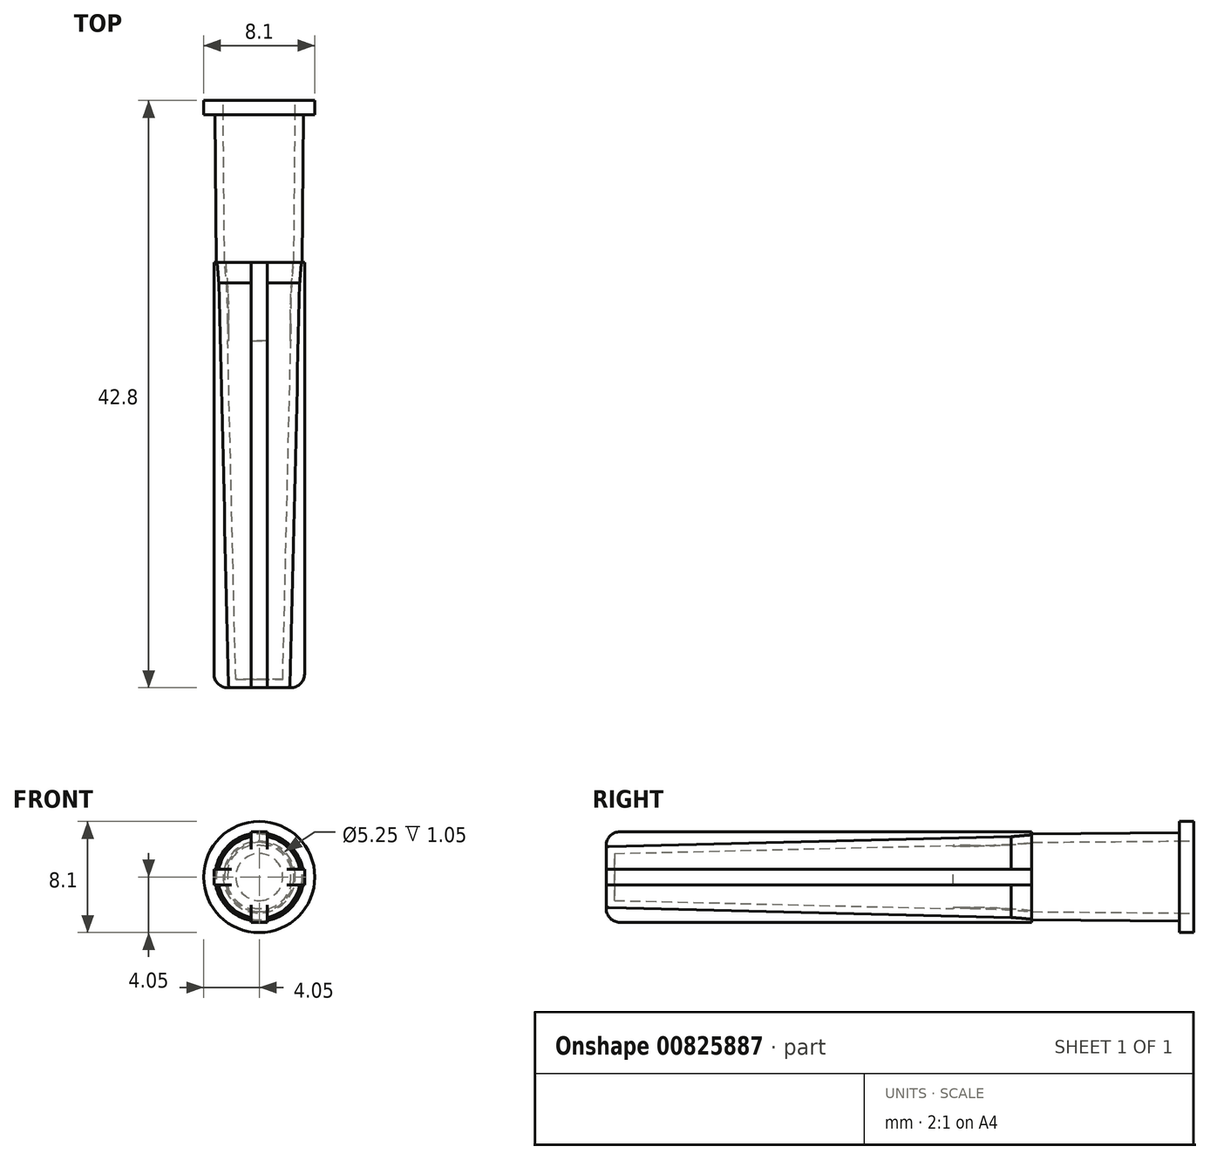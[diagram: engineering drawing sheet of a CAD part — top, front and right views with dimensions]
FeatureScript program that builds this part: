
annotation { "Feature Type Name" : "Feature", "Feature Type Description" : "" }
export const myFeature = defineFeature(function(context is Context, id is Id, definition is map)
    precondition{}
    {
        {
            var Q0;
            Q0=qCreatedBy(makeId("Front.planeOp"),FACE);
            var sketch = newSketch(context, id + "F0", { "sketchPlane" : qUnion([Q0])});
            skCircle(sketch, "E0", {"center": v(0, 0) * mm, "radius": 3.23 * mm});
            skSolve(sketch);
        }
        {
            var Q0;
            Q0=qCreatedBy(makeId("Front.planeOp"),FACE);
            cPlane(context, id + "F1", {"entities" : qUnion([Q0]), "cplaneType" : CPlaneType.OFFSET, "offset" : 10.75 * mm, "width" : 150 * mm, "height" : 150 * mm});
        }
        {
            var Q0;
            Q0=qCreatedBy(id+"F1.planeOp",FACE);
            var sketch = newSketch(context, id + "F2", { "sketchPlane" : qUnion([Q0])});
            skCircle(sketch, "E1", {"center": v(0, 0) * mm, "radius": 3.12 * mm});
            skSolve(sketch);
        }
        {
            var Q0;
            Q0=makeQuery(id+"F0.imprint","IMPRINT",FACE,{"disambiguationData":[TD([[makeQuery(id+"F0.imprint","IMPRINT",EDGE,{"derivedFrom":sQuery(id+"F0.wireOp",EDGE,"E0")}),1.0]])]});
            var Q1;
            Q1=makeQuery(id+"F2.imprint","IMPRINT",FACE,{"disambiguationData":[TD([[makeQuery(id+"F2.imprint","IMPRINT",EDGE,{"derivedFrom":sQuery(id+"F2.wireOp",EDGE,"E1")}),1.0]])]});
            loft(context, id + "F3", {"sheetProfilesArray" : [{ "sheetProfileEntities" : qUnion([Q0]) }, { "sheetProfileEntities" : qUnion([Q1]) }]});
        }
        {
            var Q0;
            Q0=makeQuery(id+"F3.opLoft","CAP_FACE",FACE,{"disambiguationData":[OSD([makeQuery(id+"F2.imprint","IMPRINT",FACE,{"disambiguationData":[TD([[makeQuery(id+"F2.imprint","IMPRINT",EDGE,{"derivedFrom":sQuery(id+"F2.wireOp",EDGE,"E1")}),1.0]])]})])],"isStart":true});
            cPlane(context, id + "F4", {"entities" : qUnion([Q0]), "cplaneType" : CPlaneType.OFFSET, "offset" : 1.5 * mm, "width" : 150 * mm, "height" : 150 * mm});
        }
        {
            var Q0;
            Q0=qCreatedBy(id+"F4.planeOp",FACE);
            var sketch = newSketch(context, id + "F5", { "sketchPlane" : qUnion([Q0])});
            skCircle(sketch, "E2", {"center": v(0, 0) * mm, "radius": 3 * mm});
            skSolve(sketch);
        }
        {
            var Q1;
            Q1=makeQuery(id+"F3.opLoft","CAP_FACE",FACE,{"disambiguationData":[OSD([makeQuery(id+"F2.imprint","IMPRINT",FACE,{"disambiguationData":[TD([[makeQuery(id+"F2.imprint","IMPRINT",EDGE,{"derivedFrom":sQuery(id+"F2.wireOp",EDGE,"E1")}),1.0]])]})])],"isStart":true});
            var Q2;
            Q2=makeQuery(id+"F5.imprint","IMPRINT",FACE,{"disambiguationData":[TD([[makeQuery(id+"F5.imprint","IMPRINT",EDGE,{"derivedFrom":sQuery(id+"F5.wireOp",EDGE,"E2")}),1.0]])]});
            loft(context, id + "F6", {"operationType" : NewBodyOperationType.ADD, "sheetProfilesArray" : [{ "sheetProfileEntities" : qUnion([Q1]) }, { "sheetProfileEntities" : qUnion([Q2]) }]});
        }
        {
            var Q0;
            Q0=makeQuery(id+"F6.opLoft","CAP_FACE",FACE,{"disambiguationData":[OSD([makeQuery(id+"F5.imprint","IMPRINT",FACE,{"disambiguationData":[TD([[makeQuery(id+"F5.imprint","IMPRINT",EDGE,{"derivedFrom":sQuery(id+"F5.wireOp",EDGE,"E2")}),1.0]])]})])],"isStart":true});
            cPlane(context, id + "F7", {"entities" : qUnion([Q0]), "cplaneType" : CPlaneType.OFFSET, "offset" : 29.5 * mm, "width" : 150 * mm, "height" : 150 * mm});
        }
        {
            var Q0;
            Q0=qCreatedBy(id+"F7.planeOp",FACE);
            var sketch = newSketch(context, id + "F8", { "sketchPlane" : qUnion([Q0])});
            skCircle(sketch, "E3", {"center": v(0, 0) * mm, "radius": 2.3 * mm});
            skSolve(sketch);
        }
        {
            var Q1;
            Q1=makeQuery(id+"F6.opLoft","CAP_FACE",FACE,{"disambiguationData":[OSD([makeQuery(id+"F5.imprint","IMPRINT",FACE,{"disambiguationData":[TD([[makeQuery(id+"F5.imprint","IMPRINT",EDGE,{"derivedFrom":sQuery(id+"F5.wireOp",EDGE,"E2")}),1.0]])]})])],"isStart":true});
            var Q2;
            Q2=makeQuery(id+"F8.imprint","IMPRINT",FACE,{"disambiguationData":[TD([[makeQuery(id+"F8.imprint","IMPRINT",EDGE,{"derivedFrom":sQuery(id+"F8.wireOp",EDGE,"E3")}),1.0]])]});
            loft(context, id + "F9", {"operationType" : NewBodyOperationType.ADD, "sheetProfilesArray" : [{ "sheetProfileEntities" : qUnion([Q1]) }, { "sheetProfileEntities" : qUnion([Q2]) }]});
        }
        {
            var Q0;
            Q0=makeQuery(id+"F3.opLoft","CAP_FACE",FACE,{"disambiguationData":[OSD([makeQuery(id+"F0.imprint","IMPRINT",FACE,{"disambiguationData":[TD([[makeQuery(id+"F0.imprint","IMPRINT",EDGE,{"derivedFrom":sQuery(id+"F0.wireOp",EDGE,"E0")}),1.0]])]})])],"isStart":true});
            shell(context, id + "F10", {"entities" : qUnion([Q0]), "thickness" : .6 * mm});
        }
        {
            var Q0;
            Q0=makeQuery(id+"F9.opLoft","CAP_FACE",FACE,{"disambiguationData":[OSD([makeQuery(id+"F8.imprint","IMPRINT",FACE,{"disambiguationData":[TD([[makeQuery(id+"F8.imprint","IMPRINT",EDGE,{"derivedFrom":sQuery(id+"F8.wireOp",EDGE,"E3")}),1.0]])]})])],"isStart":true});
            var sketch = newSketch(context, id + "F11", { "sketchPlane" : qUnion([Q0])});
            skPoint(sketch, "E4.middle", {"position": v(0, 0) * mm});
            skArc(sketch, "E5", {"start": v(0.58, 2.23) * mm, "mid": v(0, 2.3) * mm, "end": v(-0.57, 2.23) * mm});
            skLineSegment(sketch, "E6.bottom", {"start": v(0.57, 3.3) * mm, "end": v(-0.58, 3.3) * mm});
            skLineSegment(sketch, "E6.left", {"start": v(0.57, 3.3) * mm, "end": v(0.57, 2.23) * mm});
            skLineSegment(sketch, "E6.right", {"start": v(-0.58, 3.3) * mm, "end": v(-0.58, 2.23) * mm});
            skPoint(sketch, "E6.middle", {"position": v(0, 2.3) * mm});
            skArc(sketch, "E7.1.0", {"start": v(-2.23, 0.58) * mm, "mid": v(-2.3, 0) * mm, "end": v(-2.23, -0.57) * mm});
            skLineSegment(sketch, "E7.1.1", {"start": v(-3.3, -0.57) * mm, "end": v(-2.23, -0.57) * mm});
            skLineSegment(sketch, "E7.1.2", {"start": v(-3.3, 0.58) * mm, "end": v(-3.3, -0.57) * mm});
            skLineSegment(sketch, "E7.1.3", {"start": v(-3.3, 0.58) * mm, "end": v(-2.23, 0.58) * mm});
            skArc(sketch, "E7.2.0", {"start": v(-0.58, -2.23) * mm, "mid": v(0, -2.3) * mm, "end": v(0.57, -2.23) * mm});
            skLineSegment(sketch, "E7.2.1", {"start": v(0.57, -3.3) * mm, "end": v(0.57, -2.23) * mm});
            skLineSegment(sketch, "E7.2.2", {"start": v(-0.58, -3.3) * mm, "end": v(0.57, -3.3) * mm});
            skLineSegment(sketch, "E7.2.3", {"start": v(-0.58, -3.3) * mm, "end": v(-0.58, -2.23) * mm});
            skArc(sketch, "E7.3.0", {"start": v(2.23, -0.58) * mm, "mid": v(2.3, 0) * mm, "end": v(2.23, 0.57) * mm});
            skLineSegment(sketch, "E7.3.1", {"start": v(3.3, 0.57) * mm, "end": v(2.23, 0.57) * mm});
            skLineSegment(sketch, "E7.3.2", {"start": v(3.3, -0.58) * mm, "end": v(3.3, 0.57) * mm});
            skLineSegment(sketch, "E7.3.3", {"start": v(3.3, -0.58) * mm, "end": v(2.23, -0.58) * mm});
            skSolve(sketch);
        }
        {
            var Q0;
            Q0 = qSketchRegion(id + "F11", true);
            extrude(context, id + "F12", {"entities" : qUnion([Q0]), "operationType" : NewBodyOperationType.ADD, "oppositeDirection" : true, "depth" : 31 * mm, "offsetDistance" : 25 * mm});
        }
        {
            var Q0;
            Q0=makeQuery(id+"F12.opExtrude","CAP_EDGE",EDGE,{"disambiguationData":[OSD([sQuery(id+"F11.wireOp",EDGE,"E6.bottom")])],"isStart":true});
            var Q1;
            Q1=makeQuery(id+"F12.opExtrude","CAP_EDGE",EDGE,{"disambiguationData":[OSD([sQuery(id+"F11.wireOp",EDGE,"E7.3.2")])],"isStart":true});
            var Q2;
            Q2=makeQuery(id+"F12.opExtrude","CAP_EDGE",EDGE,{"disambiguationData":[OSD([sQuery(id+"F11.wireOp",EDGE,"E7.2.2")])],"isStart":true});
            var Q3;
            Q3=makeQuery(id+"F12.opExtrude","CAP_EDGE",EDGE,{"disambiguationData":[OSD([sQuery(id+"F11.wireOp",EDGE,"E7.1.2")])],"isStart":true});
            fillet(context, id + "F13", {"entities" : qUnion([Q0, Q1, Q2, Q3]), "radius" : 1 * mm, "tangentPropagation" : true, "allowEdgeOverflow" : false});
        }
        {
            var Q0;
            {var subQ0=sQuery(id+"F11.wireOp",EDGE,"E6.left");var subQ1=sQuery(id+"F8.wireOp",EDGE,"E3");Q0=makeQuery(id+"F12.boolean.opBoolean","SPLIT",EDGE,{"disambiguationData":[TD([makeQuery(id+"F12.opExtrude","SWEPT_FACE",FACE,{"disambiguationData":[OSD([subQ0])]})])],"derivedFrom":makeQuery(id+"F9.opLoft","MID_CAP_EDGE",EDGE,{"disambiguationData":[OSD([subQ1])],"capPos":1.0})});}
            var Q1;
            {var subQ1=sQuery(id+"F8.wireOp",EDGE,"E3");var subQ2=sQuery(id+"F11.wireOp",EDGE,"E7.2.1");Q1=makeQuery(id+"F12.boolean.opBoolean","SPLIT",EDGE,{"disambiguationData":[TD([makeQuery(id+"F12.opExtrude","SWEPT_FACE",FACE,{"disambiguationData":[OSD([subQ2])]})])],"derivedFrom":makeQuery(id+"F9.opLoft","MID_CAP_EDGE",EDGE,{"disambiguationData":[OSD([subQ1])],"capPos":1.0})});}
            var Q2;
            {var subQ0=sQuery(id+"F11.wireOp",EDGE,"E7.1.1");var subQ1=sQuery(id+"F8.wireOp",EDGE,"E3");Q2=makeQuery(id+"F12.boolean.opBoolean","SPLIT",EDGE,{"disambiguationData":[TD([makeQuery(id+"F12.opExtrude","SWEPT_FACE",FACE,{"disambiguationData":[OSD([subQ0])]})])],"derivedFrom":makeQuery(id+"F9.opLoft","MID_CAP_EDGE",EDGE,{"disambiguationData":[OSD([subQ1])],"capPos":1.0})});}
            var Q3;
            {var subQ0=sQuery(id+"F11.wireOp",EDGE,"E6.right");var subQ1=sQuery(id+"F8.wireOp",EDGE,"E3");Q3=makeQuery(id+"F12.boolean.opBoolean","SPLIT",EDGE,{"disambiguationData":[TD([makeQuery(id+"F12.opExtrude","SWEPT_FACE",FACE,{"disambiguationData":[OSD([subQ0])]})])],"derivedFrom":makeQuery(id+"F9.opLoft","MID_CAP_EDGE",EDGE,{"disambiguationData":[OSD([subQ1])],"capPos":1.0})});}
            fillet(context, id + "F14", {"entities" : qUnion([Q0, Q1, Q2, Q3]), "radius" : .2 * mm, "tangentPropagation" : true, "allowEdgeOverflow" : false});
        }
        {
            var Q0;
            Q0=makeQuery(id+"F3.opLoft","CAP_FACE",FACE,{"disambiguationData":[OSD([makeQuery(id+"F0.imprint","IMPRINT",FACE,{"disambiguationData":[TD([[makeQuery(id+"F0.imprint","IMPRINT",EDGE,{"derivedFrom":sQuery(id+"F0.wireOp",EDGE,"E0")}),1.0]])]})])],"isStart":true});
            var sketch = newSketch(context, id + "F15", { "sketchPlane" : qUnion([Q0])});
            skCircle(sketch, "E8", {"center": v(0, 0) * mm, "radius": 4.05 * mm});
            skSolve(sketch);
        }
        {
            var Q0;
            Q0 = qSketchRegion(id + "F15", true);
            extrude(context, id + "F16", {"entities" : qUnion([Q0]), "operationType" : NewBodyOperationType.ADD, "depth" : 1.05 * mm, "offsetDistance" : 25 * mm});
        }
        {
            var Q0;
            Q0=makeQuery(id+"F16.opExtrude","CAP_FACE",FACE,{"disambiguationData":[OSD([sQuery(id+"F15.wireOp",EDGE,"E8")])],"isStart":false});
            var sketch = newSketch(context, id + "F17", { "sketchPlane" : qUnion([Q0])});
            skCircle(sketch, "E9", {"center": v(0, 0) * mm, "radius": 2.62 * mm});
            skSolve(sketch);
        }
        {
            var Q0;
            Q0 = qSketchRegion(id + "F17", true);
            extrude(context, id + "F18", {"entities" : qUnion([Q0]), "operationType" : NewBodyOperationType.REMOVE, "oppositeDirection" : true, "depth" : 1.05 * mm, "offsetDistance" : 25 * mm});
        }
        {
            var Q0;
            Q0=makeQuery(id+"F12.opExtrude","CAP_EDGE",EDGE,{"disambiguationData":[OSD([sQuery(id+"F11.wireOp",EDGE,"E7.1.0")])],"isStart":false});
            var Q1;
            Q1=makeQuery(id+"F12.opExtrude","CAP_EDGE",EDGE,{"disambiguationData":[OSD([sQuery(id+"F11.wireOp",EDGE,"E7.2.0")])],"isStart":false});
            var Q2;
            Q2=makeQuery(id+"F12.opExtrude","CAP_EDGE",EDGE,{"disambiguationData":[OSD([sQuery(id+"F11.wireOp",EDGE,"E7.3.0")])],"isStart":false});
            var Q3;
            Q3=makeQuery(id+"F12.opExtrude","CAP_EDGE",EDGE,{"disambiguationData":[OSD([sQuery(id+"F11.wireOp",EDGE,"E5")])],"isStart":false});
            fillet(context, id + "F19", {"entities" : qUnion([Q0, Q1, Q2, Q3]), "radius" : 45 * mm, "tangentPropagation" : true, "allowEdgeOverflow" : false});
        }
    });
